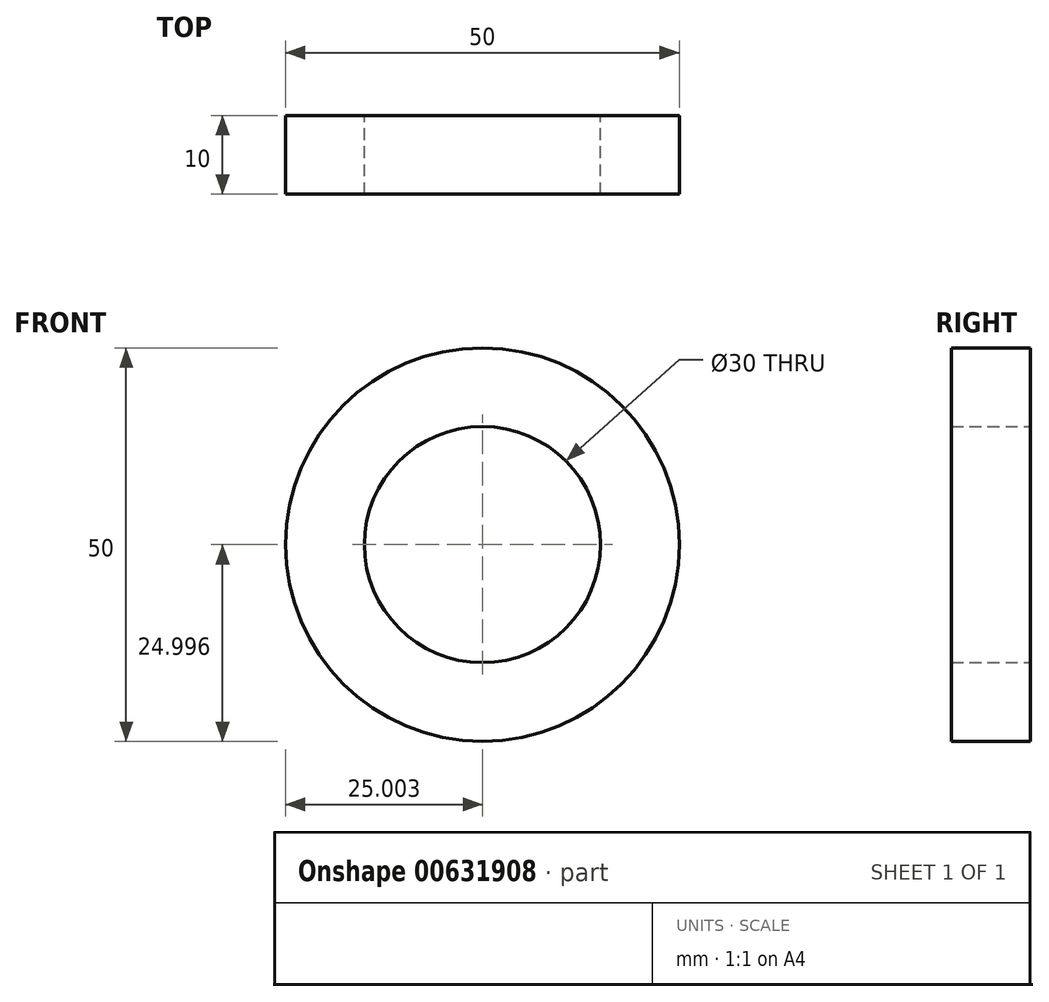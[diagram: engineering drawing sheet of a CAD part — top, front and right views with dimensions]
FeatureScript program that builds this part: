
annotation { "Feature Type Name" : "Feature", "Feature Type Description" : "" }
export const myFeature = defineFeature(function(context is Context, id is Id, definition is map)
    precondition{}
    {
        {
            var Q0;
            Q0=qCreatedBy(makeId("Front.planeOp"),FACE);
            var sketch = newSketch(context, id + "F0", { "sketchPlane" : qUnion([Q0])});
            skCircle(sketch, "E0", {"center": v(-98.2, 33.15) * mm, "radius": 15 * mm});
            skCircle(sketch, "E1", {"center": v(-98.2, 33.15) * mm, "radius": 25 * mm});
            skSolve(sketch);
        }
        {
            var Q0;
            Q0 = qSketchRegion(id + "F0", true);
            extrude(context, id + "F1", {"entities" : qUnion([Q0]), "depth" : 10 * mm, "offsetDistance" : 25 * mm});
        }
    });
